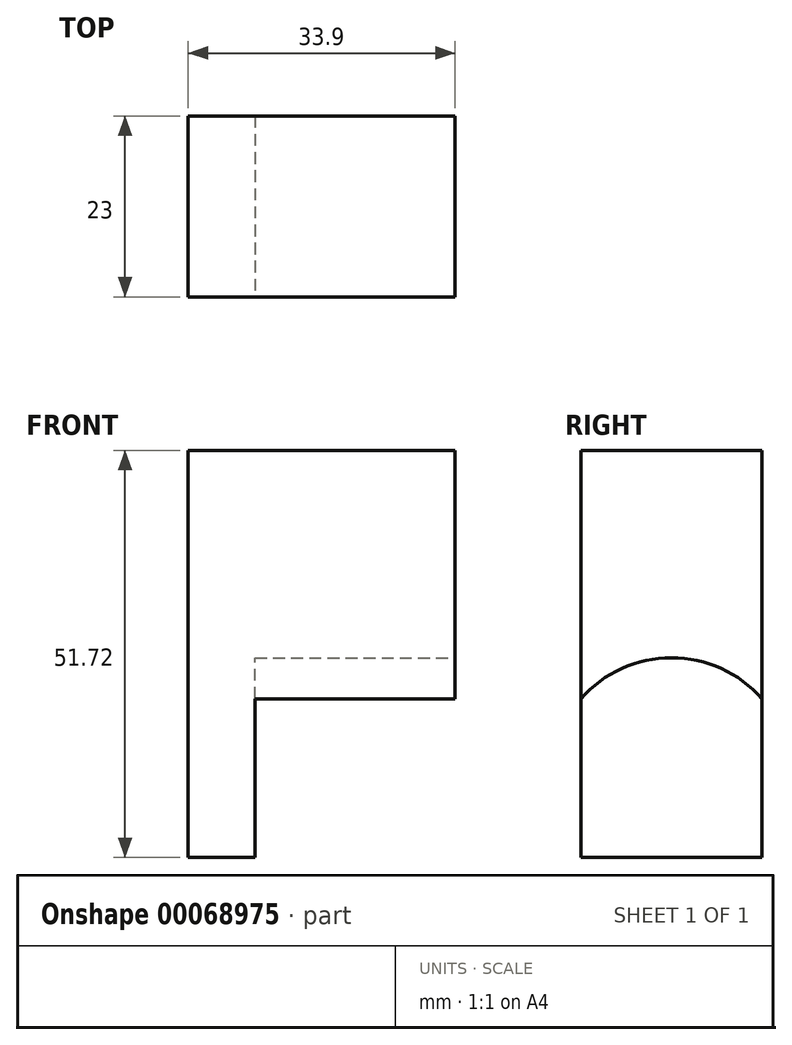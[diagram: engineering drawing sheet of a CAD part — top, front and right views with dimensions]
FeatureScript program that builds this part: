
annotation { "Feature Type Name" : "Feature", "Feature Type Description" : "" }
export const myFeature = defineFeature(function(context is Context, id is Id, definition is map)
    precondition{}
    {
        {
            var Q0;
            Q0=qCreatedBy(makeId("Front.planeOp"),FACE);
            var sketch = newSketch(context, id + "F0", { "sketchPlane" : qUnion([Q0])});
            skLineSegment(sketch, "E0", {"start": v(-41.91, 51.37) * mm, "end": v(41.91, 51.37) * mm});
            skLineSegment(sketch, "E1", {"start": v(-41.91, 25.68) * mm, "end": v(-41.91, 0) * mm});
            skLineSegment(sketch, "E2", {"start": v(41.9, 51.37) * mm, "end": v(41.9, 0) * mm});
            skLineSegment(sketch, "E3", {"start": v(0, 0) * mm, "end": v(0, 51.37) * mm, "construction": true});
            skLineSegment(sketch, "E4", {"start": v(12.34, 25.68) * mm, "end": v(-41.91, 25.68) * mm});
            skLineSegment(sketch, "E5.bottom", {"start": v(41.9, 0) * mm, "end": v(75.8, 0) * mm});
            skLineSegment(sketch, "E5.top", {"start": v(41.9, 51.72) * mm, "end": v(75.8, 51.72) * mm});
            skLineSegment(sketch, "E5.left", {"start": v(41.9, 0) * mm, "end": v(41.9, 51.72) * mm});
            skLineSegment(sketch, "E5.right", {"start": v(75.8, 0) * mm, "end": v(75.8, 51.72) * mm});
            skCircle(sketch, "E6", {"center": v(-26.35, -54.57) * mm, "radius": 12.77 * mm});
            skCircle(sketch, "E7", {"center": v(0, 25.68) * mm, "radius": 10 * mm});
            skLineSegment(sketch, "E8", {"start": v(-3.4, 16.28) * mm, "end": v(0, 0) * mm});
            skLineSegment(sketch, "E9", {"start": v(0, 0) * mm, "end": v(-9.85, 23.93) * mm});
            skLineSegment(sketch, "E10.1.0", {"start": v(6.44, 18.03) * mm, "end": v(22.24, 12.84) * mm});
            skLineSegment(sketch, "E10.1.1", {"start": v(22.24, 12.84) * mm, "end": v(-3.4, 16.28) * mm});
            skLineSegment(sketch, "E10.2.0", {"start": v(9.85, 27.44) * mm, "end": v(22.24, 38.52) * mm});
            skLineSegment(sketch, "E10.2.1", {"start": v(22.24, 38.52) * mm, "end": v(6.44, 18.03) * mm});
            skLineSegment(sketch, "E11.2.3.0", {"start": v(3.4, 35.09) * mm, "end": v(0, 51.37) * mm});
            skLineSegment(sketch, "E11.3.3.0", {"start": v(0, 51.37) * mm, "end": v(9.85, 27.44) * mm});
            skLineSegment(sketch, "E11.2.4.0", {"start": v(-6.44, 33.33) * mm, "end": v(-22.24, 38.52) * mm});
            skLineSegment(sketch, "E11.3.4.0", {"start": v(-22.24, 38.52) * mm, "end": v(3.4, 35.09) * mm});
            skLineSegment(sketch, "E11.2.5.0", {"start": v(-9.85, 23.93) * mm, "end": v(-22.24, 12.84) * mm});
            skLineSegment(sketch, "E11.3.5.0", {"start": v(-22.24, 12.84) * mm, "end": v(-6.44, 33.33) * mm});
            skPoint(sketch, "E12.orphan", {"position": v(41.91, 25.68) * mm});
            skSolve(sketch);
        }
        {
            var Q0;
            {var subQ3=sQuery(id+"F0.wireOp",EDGE,"E5.bottom");Q0=makeQuery(id+"F0.imprint","IMPRINT",FACE,{"disambiguationData":[TD([[makeQuery(id+"F0.imprint","IMPRINT",EDGE,{"derivedFrom":subQ3}),1.0]])]});}
            extrude(context, id + "F1", {"entities" : qUnion([Q0]), "oppositeDirection" : true, "depth" : 23 * mm});
        }
        {
            var Q0;
            Q0=makeQuery(id+"F1.opExtrude","SWEPT_FACE",FACE,{"disambiguationData":[OSD([sQuery(id+"F0.wireOp",EDGE,"E5.right")])]});
            var sketch = newSketch(context, id + "F2", { "sketchPlane" : qUnion([Q0])});
            skArc(sketch, "E13", {"start": v(23, 0) * mm, "mid": v(11.5, 25.4) * mm, "end": v(0, 0) * mm});
            skLineSegment(sketch, "E14", {"start": v(23, 0) * mm, "end": v(0, 0) * mm});
            skSolve(sketch);
        }
        {
            var Q0;
            Q0 = qSketchRegion(id + "F2", true);
            var Q1;
            Q1=makeQuery(id+"F1.opExtrude","SWEPT_FACE",FACE,{"disambiguationData":[OSD([sQuery(id+"F0.wireOp",EDGE,"E5.left")])]});
            extrude(context, id + "F3", {"entities" : qUnion([Q0, Q1]), "operationType" : NewBodyOperationType.REMOVE, "oppositeDirection" : true, "depth" : 25.4 * mm});
        }
    });
